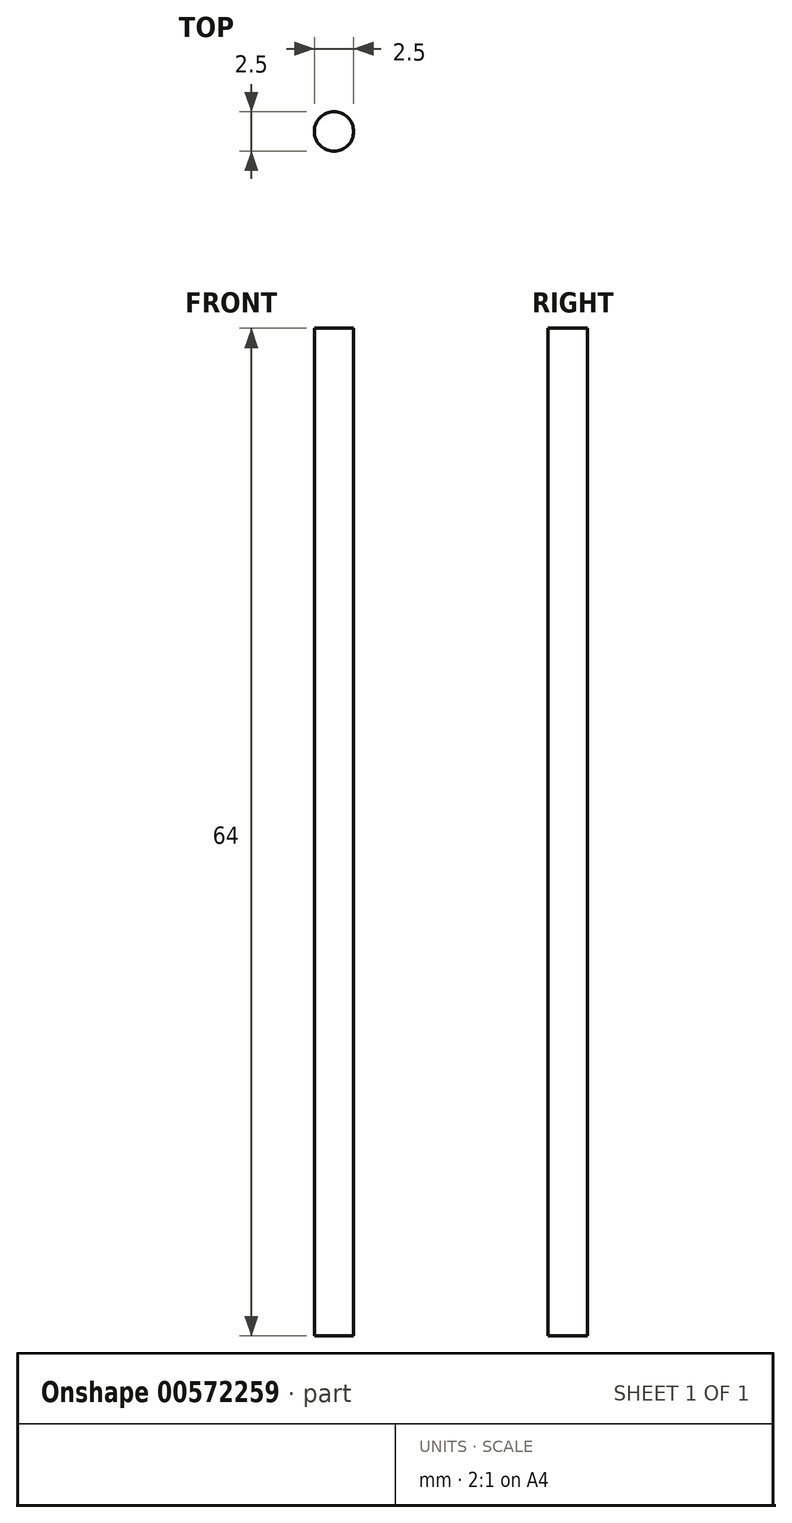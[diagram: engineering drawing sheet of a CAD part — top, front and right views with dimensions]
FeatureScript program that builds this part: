
annotation { "Feature Type Name" : "Feature", "Feature Type Description" : "" }
export const myFeature = defineFeature(function(context is Context, id is Id, definition is map)
    precondition{}
    {
        {
            var Q0;
            Q0=qCreatedBy(makeId("Top.planeOp"),FACE);
            var sketch = newSketch(context, id + "F0", { "sketchPlane" : qUnion([Q0])});
            skCircle(sketch, "E0", {"center": v(0, 0) * mm, "radius": 1.25 * mm});
            skSolve(sketch);
        }
        {
            var Q0;
            Q0 = qSketchRegion(id + "F0", true);
            extrude(context, id + "F1", {"entities" : qUnion([Q0]), "depth" : 64 * mm, "offsetDistance" : 25 * mm});
        }
    });
